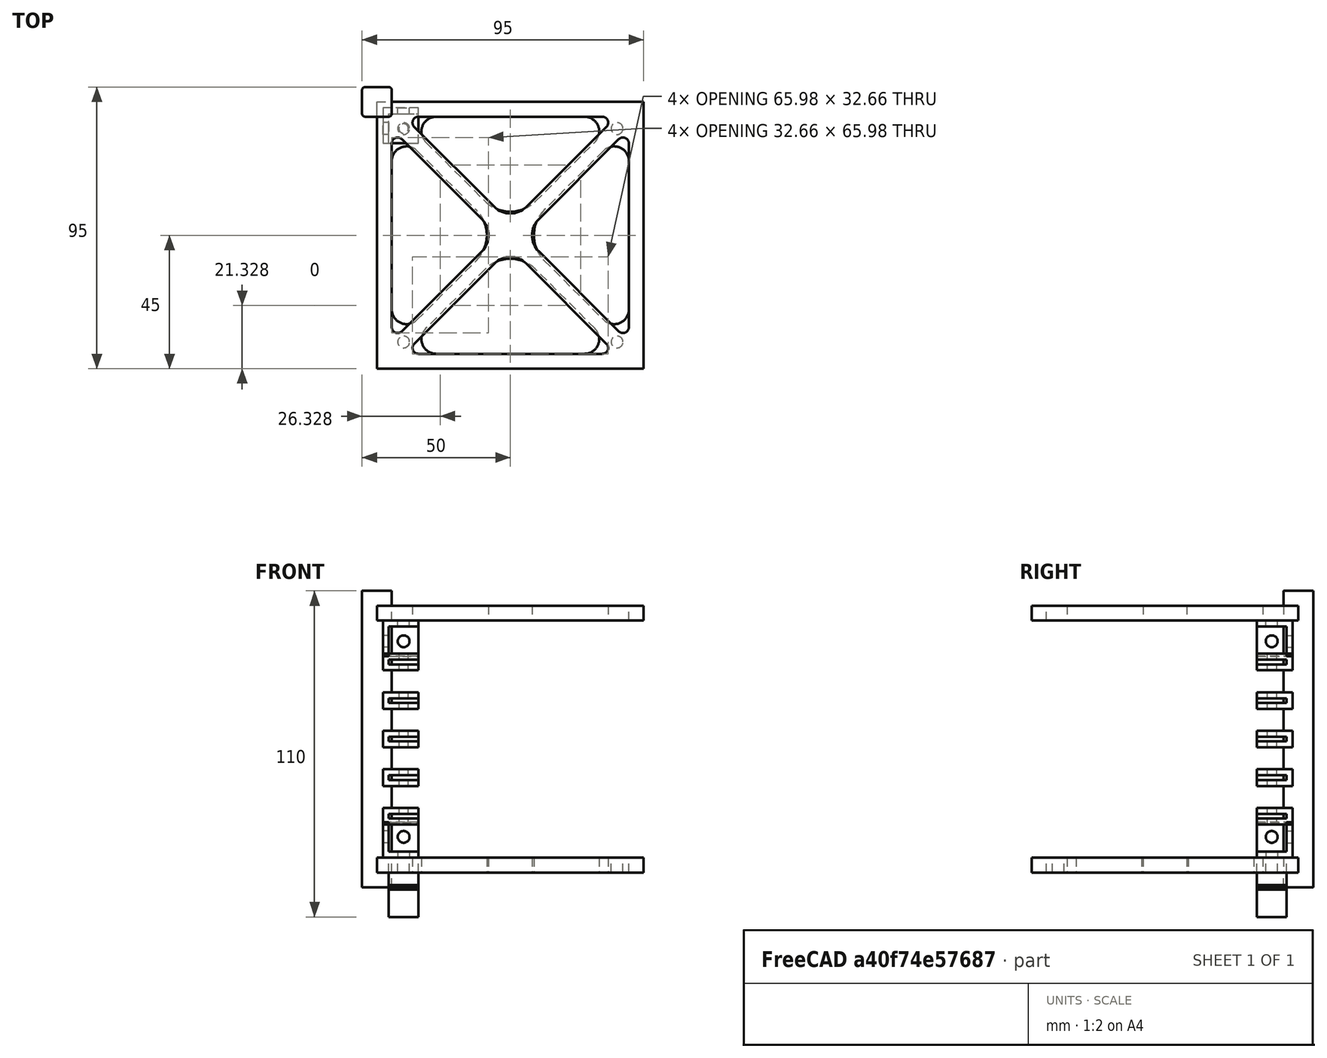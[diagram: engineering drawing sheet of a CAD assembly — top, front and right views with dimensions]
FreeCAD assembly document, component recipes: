
FREECAD ASSEMBLY — COMPONENT RECIPES ("cube")

This assembly document has 18 components, labeled P0..P17 below (a component is one placed body or linked part). 18 of them carry a construction recipe — the FreeCAD feature program that regenerates the part from scratch, quoted from this document or its linked companion documents; the rest are supplied as boundary geometry only. No exploded tour is included for this assembly.
COMPONENT P0 — recipe-attached ("BottomCutout", modeled in this document).
Construction recipe (the document's own serialized feature program — sketch geometry with constraints, then the solid features built on it; lengths are millimeters unless a unit is written):

FEATURE [Sketcher::SketchObject] Sketch
  FullyConstrained = true
  MapMode = 5
  Support = -> [XY_Plane001]
  sketch-geometry (28):
    g0: LineSegment StartX=-45 StartY=45 StartZ=0 EndX=45 EndY=45 EndZ=0
    g1: LineSegment StartX=45 StartY=45 StartZ=0 EndX=45 EndY=-45 EndZ=0
    g2: LineSegment StartX=45 StartY=-45 StartZ=0 EndX=-45 EndY=-45 EndZ=0
    g3: LineSegment StartX=-45 StartY=-45 StartZ=0 EndX=-45 EndY=45 EndZ=0
    g4: LineSegment StartX=-31 StartY=40 StartZ=0 EndX=31 EndY=40 EndZ=0
    g5: LineSegment StartX=-31 StartY=-40 StartZ=0 EndX=31 EndY=-40 EndZ=0
    g6: LineSegment StartX=-40 StartY=31 StartZ=0 EndX=-40 EndY=-31 EndZ=0
    g7: LineSegment StartX=40 StartY=31 StartZ=0 EndX=40 EndY=-31 EndZ=0
    g8: LineSegment StartX=-36.5858 StartY=32.4142 StartZ=0 EndX=-9.58579 EndY=5.41421 EndZ=0
    g9: LineSegment StartX=-32.4142 StartY=36.5858 StartZ=0 EndX=-5.41421 EndY=9.58579 EndZ=0
    g10: LineSegment StartX=5.41421 StartY=9.58579 StartZ=0 EndX=32.4142 EndY=36.5858 EndZ=0
    g11: LineSegment StartX=36.5858 StartY=32.4142 StartZ=0 EndX=9.58579 EndY=5.41421 EndZ=0
    g12: LineSegment StartX=9.58579 StartY=-5.41421 StartZ=0 EndX=36.5858 EndY=-32.4142 EndZ=0
    g13: LineSegment StartX=32.4142 StartY=-36.5858 StartZ=0 EndX=5.41421 EndY=-9.58579 EndZ=0
    g14: LineSegment StartX=-5.41421 StartY=-9.58579 StartZ=0 EndX=-32.4142 EndY=-36.5858 EndZ=0
    g15: LineSegment StartX=-36.5858 StartY=-32.4142 StartZ=0 EndX=-9.58579 EndY=-5.41421 EndZ=0
    g16: ArcOfCircle CenterX=38 CenterY=31 CenterZ=0 NormalX=0 NormalY=0 NormalZ=1 AngleXU=0 Radius=2 StartAngle=0 EndAngle=2.35619
    g17: ArcOfCircle CenterX=38 CenterY=-31 CenterZ=0 NormalX=0 NormalY=0 NormalZ=1 AngleXU=0 Radius=2 StartAngle=3.92699 EndAngle=6.28319
    g18: ArcOfCircle CenterX=31 CenterY=-38 CenterZ=0 NormalX=0 NormalY=0 NormalZ=1 AngleXU=0 Radius=2 StartAngle=4.71239 EndAngle=7.06858
    g19: ArcOfCircle CenterX=-31 CenterY=-38 CenterZ=0 NormalX=0 NormalY=0 NormalZ=1 AngleXU=0 Radius=2 StartAngle=2.35619 EndAngle=4.71239
    g20: ArcOfCircle CenterX=-38 CenterY=-31 CenterZ=0 NormalX=0 NormalY=0 NormalZ=1 AngleXU=0 Radius=2 StartAngle=3.14159 EndAngle=5.49779
    g21: ArcOfCircle CenterX=-38 CenterY=31 CenterZ=0 NormalX=0 NormalY=0 NormalZ=1 AngleXU=0 Radius=2 StartAngle=0.785398 EndAngle=3.14159
    g22: ArcOfCircle CenterX=-31 CenterY=38 CenterZ=0 NormalX=0 NormalY=0 NormalZ=1 AngleXU=0 Radius=2 StartAngle=1.5708 EndAngle=3.92699
    g23: ArcOfCircle CenterX=31 CenterY=38 CenterZ=0 NormalX=0 NormalY=0 NormalZ=1 AngleXU=0 Radius=2 StartAngle=5.49779 EndAngle=7.85398
    g24: ArcOfCircle CenterX=-15 CenterY=0 CenterZ=0 NormalX=0 NormalY=0 NormalZ=1 AngleXU=0 Radius=7.65685 StartAngle=5.49779 EndAngle=7.06858
    g25: ArcOfCircle CenterX=0 CenterY=15 CenterZ=0 NormalX=0 NormalY=0 NormalZ=1 AngleXU=0 Radius=7.65685 StartAngle=3.92699 EndAngle=5.49779
    g26: ArcOfCircle CenterX=15 CenterY=0 CenterZ=0 NormalX=0 NormalY=0 NormalZ=1 AngleXU=0 Radius=7.65685 StartAngle=2.35619 EndAngle=3.92699
    g27: ArcOfCircle CenterX=-6e-16 CenterY=-15 CenterZ=0 NormalX=0 NormalY=0 NormalZ=1 AngleXU=0 Radius=7.65685 StartAngle=0.785398 EndAngle=2.35619
  constraints (67):
    c: Coincident(g0,g1)
    c: Coincident(g1,g2)
    c: Coincident(g2,g3)
    c: Coincident(g3,g0)
    c: Horizontal(g0)
    c: Horizontal(g2)
    c: Vertical(g1)
    c: Vertical(g3)
    c: Symmetric(g0,g1,g-1)
    c: Equal(g2,g1)
    c: Horizontal(g4)
    c: Horizontal(g5)
    c: Vertical(g6)
    c: Vertical(g7)
    c: DistanceY(g3,g3) = 90
    c: Parallel(g8,g9)
    c: Parallel(g9,g12)
    c: Parallel(g12,g13)
    c: Parallel(g15,g14)
    c: Parallel(g14,g10)
    c: Parallel(g10,g11)
    c: Tangent(g11,g16) = -1.5708
    c: Tangent(g7,g16) = 1.5708
    c: Tangent(g12,g17) = -1.5708
    c: Tangent(g7,g17) = 1.5708
    c: Tangent(g13,g18) = -1.5708
    c: Tangent(g5,g18) = -1.5708
    c: Tangent(g14,g19) = -1.5708
    c: Tangent(g5,g19) = -1.5708
    c: Tangent(g15,g20) = -1.5708
    c: Tangent(g6,g20) = -1.5708
    c: Tangent(g6,g21) = -1.5708
    c: Tangent(g8,g21) = 1.5708
    c: Tangent(g9,g22) = -1.5708
    c: Tangent(g4,g22) = 1.5708
    c: Tangent(g4,g23) = 1.5708
    c: Tangent(g10,g23) = -1.5708
    c: Tangent(g8,g24) = 1.5708
    c: Tangent(g15,g24) = -1.5708
    c: Tangent(g9,g25) = -1.5708
    c: Tangent(g10,g25) = -1.5708
    c: Tangent(g11,g26) = -1.5708
    c: Tangent(g12,g26) = -1.5708
    c: Tangent(g13,g27) = -1.5708
    c: Tangent(g14,g27) = -1.5708
    c: Symmetric(g8,g12,g-1)
    c: PointOnObject(g24,g-1)
    c: PointOnObject(g26,g-1)
    c: Symmetric(g10,g14,g-1)
    c: Symmetric(g21,g17,g-1)
    c: Symmetric(g19,g23,g-1)
    c: Vertical(g21,g20)
    c: Horizontal(g18,g19)
    c: Vertical(g15,g8)
    c: Equal(g25,g24)
    c: Equal(g26,g27)
    c: PointOnObject(g25,g-2)
    c: Horizontal(g16,g21)
    c: Equal(g4,g5)
    c: Equal(g6,g5)
    c: DistanceX(g2,g6) = 5
    c: DistanceY(g2,g5) = 5
    c: DistanceX(g18,g1) = 14
    c: DistanceX(g26,g1) = 30
    c: DistanceY(g1,g18) = 7
    c: Perpendicular(g11,g8)
    c: DistanceX(g17,g1) = 7
FEATURE [PartDesign::Pad] Pad
  Direction = (1,1,1)
  Length = 5
  Length2 = 100
  Profile = -> Sketch
  Refine = true
  Type = 0
FEATURE [PartDesign::Body] Body  label="BottomCutout"
  Group = -> [Sketch,Pad]
  Origin = -> Origin001
  Placement = pos=(0,0,5) rot=(0,0,1;0rad)
  Tip = -> Pad
COMPONENT P1 — recipe-attached ("BottomCorner", modeled in this document).
Construction recipe (the document's own serialized feature program — sketch geometry with constraints, then the solid features built on it; lengths are millimeters unless a unit is written):

FEATURE [Sketcher::SketchObject] Sketch003
  FullyConstrained = true
  MapMode = 5
  Support = -> [XY_Plane004]
  sketch-geometry (4):
    g0: LineSegment StartX=-43 StartY=31 StartZ=0 EndX=-31 EndY=31 EndZ=0
    g1: LineSegment StartX=-31 StartY=31 StartZ=0 EndX=-31 EndY=43 EndZ=0
    g2: LineSegment StartX=-31 StartY=43 StartZ=0 EndX=-43 EndY=43 EndZ=0
    g3: LineSegment StartX=-43 StartY=43 StartZ=0 EndX=-43 EndY=31 EndZ=0
  constraints (12):
    c: Coincident(g1,g2)
    c: Coincident(g2,g3)
    c: Coincident(g3,g0)
    c: Horizontal(g0)
    c: Horizontal(g2)
    c: Vertical(g1)
    c: Vertical(g3)
    c: Equal(g3,g0)
    c: Coincident(g0,g1)
    c: Distance(g1,g0) = 12
    c: DistanceY(g-1,g0) = 31
    c: DistanceX(g0,g-1) = 31
FEATURE [PartDesign::Pad] Pad002
  Direction = (1,1,1)
  Length = 12
  Length2 = 100
  Profile = -> Sketch003
  Refine = true
  Reversed = true
  Type = 0
FEATURE [PartDesign::Boolean] Boolean001
  BaseFeature = -> Pad002
  Group = -> [Body003]
  Refine = true
  Type = 1
FEATURE [Sketcher::SketchObject] Sketch005  label="yCornerHoleSketch"
  FullyConstrained = true
  MapMode = 5
  Placement = pos=(0,0,0) rot=(1,0,0;1.5708rad)
  Support = -> [XZ_Plane004]
  sketch-geometry (1):
    g0: Circle CenterX=-36 CenterY=-5 CenterZ=0 NormalX=0 NormalY=0 NormalZ=1 AngleXU=0 Radius=2
  constraints (3):
    c: DistanceY(g0,g-1) = 5
    c: DistanceX(g-1,g0) = -36
    c: Radius(g0) = 2
FEATURE [PartDesign::Hole] Hole  label="yCornerHole"
  BaseFeature = -> Boolean001
  Depth = 25
  DepthType = 1
  Diameter = 4
  DrillForDepth = false
  DrillPoint = 1
  DrillPointAngle = 118
  HoleCutCountersinkAngle = 90
  HoleCutCustomValues = false
  HoleCutDepth = 0
  HoleCutDiameter = 4.1
  HoleCutType = 2
  ModelActualThread = false
  Profile = -> Sketch005
  Refine = true
  Tapered = false
  TaperedAngle = 90
  ThreadAngle = 0
  ThreadClass = 0
  ThreadCutOffInner = 0
  ThreadCutOffOuter = 0
  ThreadDirection = 0
  ThreadFit = 0
  ThreadPitch = 0
  ThreadSize = 0
  ThreadType = 0
  Threaded = false
FEATURE [Sketcher::SketchObject] Sketch006  label="zConerHoleSketch"
  FullyConstrained = true
  MapMode = 5
  Placement = pos=(0,0,-10) rot=(0,0,1;0rad)
  Support = -> [Hole]
  sketch-geometry (1):
    g0: Circle CenterX=-36 CenterY=36 CenterZ=0 NormalX=0 NormalY=0 NormalZ=1 AngleXU=0 Radius=2
  constraints (3):
    c: DistanceX(g-1,g0) = -36
    c: DistanceY(g-1,g0) = 36
    c: Radius(g0) = 2
FEATURE [PartDesign::Hole] Hole001  label="zCornerHole"
  BaseFeature = -> Hole
  Depth = 25
  DepthType = 0
  Diameter = 4
  DrillForDepth = false
  DrillPoint = 1
  DrillPointAngle = 118
  HoleCutCountersinkAngle = 90
  HoleCutCustomValues = false
  HoleCutDepth = 0
  HoleCutDiameter = 6.1
  HoleCutType = 0
  ModelActualThread = false
  Profile = -> Sketch006
  Refine = true
  Tapered = false
  TaperedAngle = 90
  ThreadAngle = 0
  ThreadClass = 0
  ThreadCutOffInner = 0
  ThreadCutOffOuter = 0
  ThreadDirection = 0
  ThreadFit = 0
  ThreadPitch = 0
  ThreadSize = 0
  ThreadType = 0
  Threaded = false
FEATURE [Sketcher::SketchObject] Sketch007  label="xCornerHoleSketch"
  FullyConstrained = true
  MapMode = 5
  Placement = pos=(-41,0,0) rot=(0.57735,0.57735,0.57735;2.0944rad)
  Support = -> [Hole001]
  sketch-geometry (1):
    g0: Circle CenterX=36 CenterY=-5 CenterZ=0 NormalX=0 NormalY=0 NormalZ=1 AngleXU=0 Radius=2
  constraints (3):
    c: DistanceY(g0,g-1) = 5
    c: DistanceX(g-1,g0) = 36
    c: Radius(g0) = 2
FEATURE [PartDesign::Hole] Hole002  label="xCornerHole"
  BaseFeature = -> Hole001
  Depth = 25
  DepthType = 0
  Diameter = 4
  DrillForDepth = false
  DrillPoint = 1
  DrillPointAngle = 118
  HoleCutCountersinkAngle = 90
  HoleCutCustomValues = false
  HoleCutDepth = 0
  HoleCutDiameter = 6.1
  HoleCutType = 0
  ModelActualThread = false
  Profile = -> Sketch007
  Refine = true
  Tapered = false
  TaperedAngle = 90
  ThreadAngle = 0
  ThreadClass = 0
  ThreadCutOffInner = 0
  ThreadCutOffOuter = 0
  ThreadDirection = 0
  ThreadFit = 0
  ThreadPitch = 0
  ThreadSize = 0
  ThreadType = 0
  Threaded = false
FEATURE [PartDesign::Body] Body002  label="BottomCorner"
  Group = -> [Sketch003,Pad002,Boolean001,Sketch005,Hole,Sketch006,Hole001,Sketch007,Hole002]
  Origin = -> Origin004
  Placement = pos=(0,0,22) rot=(0,0,1;0rad)
  Tip = -> Hole002
COMPONENT P2 — recipe-attached ("Neg_Corner", modeled in this document).
Construction recipe (the document's own serialized feature program — sketch geometry with constraints, then the solid features built on it; lengths are millimeters unless a unit is written):

FEATURE [Sketcher::SketchObject] Sketch002
  FullyConstrained = true
  MapMode = 5
  Support = -> [XY_Plane005]
  sketch-geometry (4):
    g0: LineSegment StartX=-41 StartY=41 StartZ=0 EndX=-31 EndY=41 EndZ=0
    g1: LineSegment StartX=-31 StartY=41 StartZ=0 EndX=-31 EndY=31 EndZ=0
    g2: LineSegment StartX=-31 StartY=31 StartZ=0 EndX=-41 EndY=31 EndZ=0
    g3: LineSegment StartX=-41 StartY=31 StartZ=0 EndX=-41 EndY=41 EndZ=0
  constraints (12):
    c: Coincident(g0,g1)
    c: Coincident(g1,g2)
    c: Coincident(g2,g3)
    c: Coincident(g3,g0)
    c: Horizontal(g0)
    c: Horizontal(g2)
    c: Vertical(g1)
    c: Vertical(g3)
    c: Equal(g3,g2)
    c: Distance(g1) = 10
    c: DistanceX(g-1,g2) = -41
    c: DistanceY(g-1,g2) = 31
FEATURE [PartDesign::Pad] Pad003
  Direction = (1,1,1)
  Length = 10
  Length2 = 100
  Profile = -> Sketch002
  Refine = true
  Reversed = true
  Type = 0
FEATURE [PartDesign::Body] Body003  label="Neg_Corner"
  Group = -> [Sketch002,Pad003]
  Origin = -> Origin005
  Tip = -> Pad003
COMPONENT P3 — recipe-attached ("TopCutout", modeled in this document).
Construction recipe (the document's own serialized feature program — sketch geometry with constraints, then the solid features built on it; lengths are millimeters unless a unit is written):

FEATURE [Sketcher::SketchObject] Sketch010
  FullyConstrained = true
  MapMode = 5
  Support = -> [XY_Plane008]
  sketch-geometry (28):
    g0: LineSegment StartX=-45 StartY=45 StartZ=0 EndX=45 EndY=45 EndZ=0
    g1: LineSegment StartX=45 StartY=45 StartZ=0 EndX=45 EndY=-45 EndZ=0
    g2: LineSegment StartX=45 StartY=-45 StartZ=0 EndX=-45 EndY=-45 EndZ=0
    g3: LineSegment StartX=-45 StartY=-45 StartZ=0 EndX=-45 EndY=45 EndZ=0
    g4: LineSegment StartX=-31 StartY=40 StartZ=0 EndX=31 EndY=40 EndZ=0
    g5: LineSegment StartX=-31 StartY=-40 StartZ=0 EndX=31 EndY=-40 EndZ=0
    g6: LineSegment StartX=-40 StartY=31 StartZ=0 EndX=-40 EndY=-31 EndZ=0
    g7: LineSegment StartX=40 StartY=31 StartZ=0 EndX=40 EndY=-31 EndZ=0
    g8: LineSegment StartX=-36.5858 StartY=32.4142 StartZ=0 EndX=-9.58579 EndY=5.41421 EndZ=0
    g9: LineSegment StartX=-32.4142 StartY=36.5858 StartZ=0 EndX=-5.41421 EndY=9.58579 EndZ=0
    g10: LineSegment StartX=5.41421 StartY=9.58579 StartZ=0 EndX=32.4142 EndY=36.5858 EndZ=0
    g11: LineSegment StartX=36.5858 StartY=32.4142 StartZ=0 EndX=9.58579 EndY=5.41421 EndZ=0
    g12: LineSegment StartX=9.58579 StartY=-5.41421 StartZ=0 EndX=36.5858 EndY=-32.4142 EndZ=0
    g13: LineSegment StartX=32.4142 StartY=-36.5858 StartZ=0 EndX=5.41421 EndY=-9.58579 EndZ=0
    g14: LineSegment StartX=-5.41421 StartY=-9.58579 StartZ=0 EndX=-32.4142 EndY=-36.5858 EndZ=0
    g15: LineSegment StartX=-36.5858 StartY=-32.4142 StartZ=0 EndX=-9.58579 EndY=-5.41421 EndZ=0
    g16: ArcOfCircle CenterX=38 CenterY=31 CenterZ=0 NormalX=0 NormalY=0 NormalZ=1 AngleXU=0 Radius=2 StartAngle=0 EndAngle=2.35619
    g17: ArcOfCircle CenterX=38 CenterY=-31 CenterZ=0 NormalX=0 NormalY=0 NormalZ=1 AngleXU=0 Radius=2 StartAngle=3.92699 EndAngle=6.28319
    g18: ArcOfCircle CenterX=31 CenterY=-38 CenterZ=0 NormalX=0 NormalY=0 NormalZ=1 AngleXU=0 Radius=2 StartAngle=4.71239 EndAngle=7.06858
    g19: ArcOfCircle CenterX=-31 CenterY=-38 CenterZ=0 NormalX=0 NormalY=0 NormalZ=1 AngleXU=0 Radius=2 StartAngle=2.35619 EndAngle=4.71239
    g20: ArcOfCircle CenterX=-38 CenterY=-31 CenterZ=0 NormalX=0 NormalY=0 NormalZ=1 AngleXU=0 Radius=2 StartAngle=3.14159 EndAngle=5.49779
    g21: ArcOfCircle CenterX=-38 CenterY=31 CenterZ=0 NormalX=0 NormalY=0 NormalZ=1 AngleXU=0 Radius=2 StartAngle=0.785398 EndAngle=3.14159
    g22: ArcOfCircle CenterX=-31 CenterY=38 CenterZ=0 NormalX=0 NormalY=0 NormalZ=1 AngleXU=0 Radius=2 StartAngle=1.5708 EndAngle=3.92699
    g23: ArcOfCircle CenterX=31 CenterY=38 CenterZ=0 NormalX=0 NormalY=0 NormalZ=1 AngleXU=0 Radius=2 StartAngle=5.49779 EndAngle=7.85398
    g24: ArcOfCircle CenterX=-15 CenterY=0 CenterZ=0 NormalX=0 NormalY=0 NormalZ=1 AngleXU=0 Radius=7.65685 StartAngle=5.49779 EndAngle=7.06858
    g25: ArcOfCircle CenterX=0 CenterY=15 CenterZ=0 NormalX=0 NormalY=0 NormalZ=1 AngleXU=0 Radius=7.65685 StartAngle=3.92699 EndAngle=5.49779
    g26: ArcOfCircle CenterX=15 CenterY=0 CenterZ=0 NormalX=0 NormalY=0 NormalZ=1 AngleXU=0 Radius=7.65685 StartAngle=2.35619 EndAngle=3.92699
    g27: ArcOfCircle CenterX=-6e-16 CenterY=-15 CenterZ=0 NormalX=0 NormalY=0 NormalZ=1 AngleXU=0 Radius=7.65685 StartAngle=0.785398 EndAngle=2.35619
  constraints (67):
    c: Coincident(g0,g1)
    c: Coincident(g1,g2)
    c: Coincident(g2,g3)
    c: Coincident(g3,g0)
    c: Horizontal(g0)
    c: Horizontal(g2)
    c: Vertical(g1)
    c: Vertical(g3)
    c: Symmetric(g0,g1,g-1)
    c: Equal(g2,g1)
    c: Horizontal(g4)
    c: Horizontal(g5)
    c: Vertical(g6)
    c: Vertical(g7)
    c: DistanceY(g3,g3) = 90
    c: Parallel(g8,g9)
    c: Parallel(g9,g12)
    c: Parallel(g12,g13)
    c: Parallel(g15,g14)
    c: Parallel(g14,g10)
    c: Parallel(g10,g11)
    c: Tangent(g11,g16) = -1.5708
    c: Tangent(g7,g16) = 1.5708
    c: Tangent(g12,g17) = -1.5708
    c: Tangent(g7,g17) = 1.5708
    c: Tangent(g13,g18) = -1.5708
    c: Tangent(g5,g18) = -1.5708
    c: Tangent(g14,g19) = -1.5708
    c: Tangent(g5,g19) = -1.5708
    c: Tangent(g15,g20) = -1.5708
    c: Tangent(g6,g20) = -1.5708
    c: Tangent(g6,g21) = -1.5708
    c: Tangent(g8,g21) = 1.5708
    c: Tangent(g9,g22) = -1.5708
    c: Tangent(g4,g22) = 1.5708
    c: Tangent(g4,g23) = 1.5708
    c: Tangent(g10,g23) = -1.5708
    c: Tangent(g8,g24) = 1.5708
    c: Tangent(g15,g24) = -1.5708
    c: Tangent(g9,g25) = -1.5708
    c: Tangent(g10,g25) = -1.5708
    c: Tangent(g11,g26) = -1.5708
    c: Tangent(g12,g26) = -1.5708
    c: Tangent(g13,g27) = -1.5708
    c: Tangent(g14,g27) = -1.5708
    c: Symmetric(g8,g12,g-1)
    c: PointOnObject(g24,g-1)
    c: PointOnObject(g26,g-1)
    c: Symmetric(g10,g14,g-1)
    c: Symmetric(g21,g17,g-1)
    c: Symmetric(g19,g23,g-1)
    c: Vertical(g21,g20)
    c: Horizontal(g18,g19)
    c: Vertical(g15,g8)
    c: Equal(g25,g24)
    c: Equal(g26,g27)
    c: PointOnObject(g25,g-2)
    c: Horizontal(g16,g21)
    c: Equal(g4,g5)
    c: Equal(g6,g5)
    c: DistanceX(g2,g6) = 5
    c: DistanceY(g2,g5) = 5
    c: DistanceX(g18,g1) = 14
    c: DistanceX(g26,g1) = 30
    c: DistanceY(g1,g18) = 7
    c: Perpendicular(g11,g8)
    c: DistanceX(g17,g1) = 7
FEATURE [PartDesign::Pad] Pad005
  Direction = (1,1,1)
  Length = 5
  Length2 = 100
  Profile = -> Sketch010
  Refine = true
  Type = 0
FEATURE [PartDesign::Body] Body005  label="TopCutout"
  Group = -> [Sketch010,Pad005]
  Origin = -> Origin008
  Placement = pos=(0,0,90) rot=(0,0,1;0rad)
  Tip = -> Pad005
COMPONENT P4 — recipe-attached ("TopCorner", modeled in this document).
Construction recipe (the document's own serialized feature program — sketch geometry with constraints, then the solid features built on it; lengths are millimeters unless a unit is written):

FEATURE [Sketcher::SketchObject] Sketch012
  FullyConstrained = true
  MapMode = 5
  Support = -> [XY_Plane009]
  sketch-geometry (4):
    g0: LineSegment StartX=-43 StartY=31 StartZ=0 EndX=-31 EndY=31 EndZ=0
    g1: LineSegment StartX=-31 StartY=31 StartZ=0 EndX=-31 EndY=43 EndZ=0
    g2: LineSegment StartX=-31 StartY=43 StartZ=0 EndX=-43 EndY=43 EndZ=0
    g3: LineSegment StartX=-43 StartY=43 StartZ=0 EndX=-43 EndY=31 EndZ=0
  constraints (12):
    c: Coincident(g1,g2)
    c: Coincident(g2,g3)
    c: Coincident(g3,g0)
    c: Horizontal(g0)
    c: Horizontal(g2)
    c: Vertical(g1)
    c: Vertical(g3)
    c: Equal(g3,g0)
    c: Coincident(g0,g1)
    c: Distance(g1,g0) = 12
    c: DistanceY(g-1,g0) = 31
    c: DistanceX(g0,g-1) = 31
FEATURE [PartDesign::Pad] Pad006
  Direction = (1,1,1)
  Length = 12
  Length2 = 100
  Profile = -> Sketch012
  Refine = true
  Type = 0
FEATURE [PartDesign::Boolean] Boolean003
  BaseFeature = -> Pad006
  Group = -> [Body007]
  Refine = true
  Type = 1
FEATURE [Sketcher::SketchObject] Sketch013  label="yCornerHoleSketch001"
  FullyConstrained = true
  MapMode = 5
  Placement = pos=(0,0,0) rot=(1,0,0;1.5708rad)
  Support = -> [XZ_Plane009]
  sketch-geometry (1):
    g0: Circle CenterX=-36 CenterY=5 CenterZ=0 NormalX=0 NormalY=0 NormalZ=1 AngleXU=0 Radius=2
  constraints (3):
    c: DistanceY(g0,g-1) = -5
    c: DistanceX(g-1,g0) = -36
    c: Radius(g0) = 2
FEATURE [PartDesign::Hole] Hole005  label="yCornerHole001"
  BaseFeature = -> Boolean003
  Depth = 25
  DepthType = 1
  Diameter = 4
  DrillForDepth = false
  DrillPoint = 1
  DrillPointAngle = 118
  HoleCutCountersinkAngle = 90
  HoleCutCustomValues = false
  HoleCutDepth = 0
  HoleCutDiameter = 4.1
  HoleCutType = 2
  ModelActualThread = false
  Profile = -> Sketch013
  Refine = true
  Tapered = false
  TaperedAngle = 90
  ThreadAngle = 0
  ThreadClass = 0
  ThreadCutOffInner = 0
  ThreadCutOffOuter = 0
  ThreadDirection = 0
  ThreadFit = 0
  ThreadPitch = 0
  ThreadSize = 0
  ThreadType = 0
  Threaded = false
FEATURE [Sketcher::SketchObject] Sketch014  label="zConerHoleSketch001"
  FullyConstrained = true
  MapMode = 5
  Placement = pos=(0,0,10) rot=(1,0,0;3.14159rad)
  Support = -> [Hole005]
  sketch-geometry (1):
    g0: Circle CenterX=-36 CenterY=-36 CenterZ=0 NormalX=0 NormalY=0 NormalZ=1 AngleXU=0 Radius=2
  constraints (3):
    c: DistanceX(g-1,g0) = -36
    c: DistanceY(g-1,g0) = -36
    c: Radius(g0) = 2
FEATURE [PartDesign::Hole] Hole006  label="zCornerHole001"
  BaseFeature = -> Hole005
  Depth = 25
  DepthType = 0
  Diameter = 4
  DrillForDepth = false
  DrillPoint = 1
  DrillPointAngle = 118
  HoleCutCountersinkAngle = 90
  HoleCutCustomValues = false
  HoleCutDepth = 0
  HoleCutDiameter = 6.1
  HoleCutType = 0
  ModelActualThread = false
  Profile = -> Sketch014
  Refine = true
  Tapered = false
  TaperedAngle = 90
  ThreadAngle = 0
  ThreadClass = 0
  ThreadCutOffInner = 0
  ThreadCutOffOuter = 0
  ThreadDirection = 0
  ThreadFit = 0
  ThreadPitch = 0
  ThreadSize = 0
  ThreadType = 0
  Threaded = false
FEATURE [Sketcher::SketchObject] Sketch015  label="xCornerHoleSketch001"
  FullyConstrained = true
  MapMode = 5
  Placement = pos=(-41,0,0) rot=(0.57735,0.57735,0.57735;2.0944rad)
  Support = -> [Hole006]
  sketch-geometry (1):
    g0: Circle CenterX=36 CenterY=5 CenterZ=0 NormalX=0 NormalY=0 NormalZ=1 AngleXU=0 Radius=2
  constraints (3):
    c: DistanceY(g0,g-1) = -5
    c: DistanceX(g-1,g0) = 36
    c: Radius(g0) = 2
FEATURE [PartDesign::Hole] Hole007  label="xCornerHole001"
  BaseFeature = -> Hole006
  Depth = 25
  DepthType = 0
  Diameter = 4
  DrillForDepth = false
  DrillPoint = 1
  DrillPointAngle = 118
  HoleCutCountersinkAngle = 90
  HoleCutCustomValues = false
  HoleCutDepth = 0
  HoleCutDiameter = 6.1
  HoleCutType = 0
  ModelActualThread = false
  Profile = -> Sketch015
  Refine = true
  Tapered = false
  TaperedAngle = 90
  ThreadAngle = 0
  ThreadClass = 0
  ThreadCutOffInner = 0
  ThreadCutOffOuter = 0
  ThreadDirection = 0
  ThreadFit = 0
  ThreadPitch = 0
  ThreadSize = 0
  ThreadType = 0
  Threaded = false
FEATURE [PartDesign::Body] Body006  label="TopCorner"
  Group = -> [Sketch012,Pad006,Boolean003,Sketch013,Hole005,Sketch014,Hole006,Sketch015,Hole007]
  Origin = -> Origin009
  Placement = pos=(0,0,78) rot=(0,1,0;0rad)
  Tip = -> Hole007
COMPONENT P5 — recipe-attached ("Neg_Corner001", modeled in this document).
Construction recipe (the document's own serialized feature program — sketch geometry with constraints, then the solid features built on it; lengths are millimeters unless a unit is written):

FEATURE [Sketcher::SketchObject] Sketch011
  FullyConstrained = true
  MapMode = 5
  Support = -> [XY_Plane010]
  sketch-geometry (4):
    g0: LineSegment StartX=-41 StartY=41 StartZ=0 EndX=-31 EndY=41 EndZ=0
    g1: LineSegment StartX=-31 StartY=41 StartZ=0 EndX=-31 EndY=31 EndZ=0
    g2: LineSegment StartX=-31 StartY=31 StartZ=0 EndX=-41 EndY=31 EndZ=0
    g3: LineSegment StartX=-41 StartY=31 StartZ=0 EndX=-41 EndY=41 EndZ=0
  constraints (12):
    c: Coincident(g0,g1)
    c: Coincident(g1,g2)
    c: Coincident(g2,g3)
    c: Coincident(g3,g0)
    c: Horizontal(g0)
    c: Horizontal(g2)
    c: Vertical(g1)
    c: Vertical(g3)
    c: Equal(g3,g2)
    c: Distance(g1) = 10
    c: DistanceX(g-1,g2) = -41
    c: DistanceY(g-1,g2) = 31
FEATURE [PartDesign::Pad] Pad007
  Direction = (1,1,1)
  Length = 10
  Length2 = 100
  Profile = -> Sketch011
  Refine = true
  Type = 0
FEATURE [PartDesign::Body] Body007  label="Neg_Corner001"
  Group = -> [Sketch011,Pad007]
  Origin = -> Origin010
  Tip = -> Pad007
COMPONENT P6 — recipe-attached ("BoardSupport", modeled in this document).
Construction recipe (the document's own serialized feature program — sketch geometry with constraints, then the solid features built on it; lengths are millimeters unless a unit is written):

FEATURE [Sketcher::SketchObject] Sketch017
  FullyConstrained = true
  MapMode = 5
  Support = -> [XY_Plane011]
  sketch-geometry (5):
    g0: Circle CenterX=-36 CenterY=36 CenterZ=0 NormalX=0 NormalY=0 NormalZ=1 AngleXU=0 Radius=1.62
    g1: LineSegment StartX=-43 StartY=31 StartZ=0 EndX=-31 EndY=31 EndZ=0
    g2: LineSegment StartX=-31 StartY=31 StartZ=0 EndX=-31 EndY=43 EndZ=0
    g3: LineSegment StartX=-31 StartY=43 StartZ=0 EndX=-43 EndY=43 EndZ=0
    g4: LineSegment StartX=-43 StartY=43 StartZ=0 EndX=-43 EndY=31 EndZ=0
  constraints (15):
    c: Radius(g0) = 1.62
    c: Coincident(g1,g2)
    c: Coincident(g2,g3)
    c: Coincident(g3,g4)
    c: Coincident(g4,g1)
    c: Horizontal(g1)
    c: Horizontal(g3)
    c: Vertical(g2)
    c: Vertical(g4)
    c: Equal(g4,g1)
    c: Distance(g2) = 12
    c: DistanceX(g0,g-1) = 36
    c: DistanceY(g-1,g0) = 36
    c: DistanceY(g1,g0) = 5
    c: DistanceX(g0,g1) = 5
FEATURE [PartDesign::Pad] Pad009
  Direction = (1,1,1)
  Length = 5.6
  Length2 = 100
  Midplane = true
  Profile = -> Sketch017
  Refine = true
  Type = 0
FEATURE [PartDesign::Boolean] Boolean004
  BaseFeature = -> Pad009
  Group = -> [Body009]
  Refine = true
  Type = 1
FEATURE [PartDesign::Body] Body008  label="BoardSupport"
  Group = -> [Sketch017,Pad009,Boolean004]
  Origin = -> Origin011
  Placement = pos=(0,0,76) rot=(0,0,1;0rad)
  Tip = -> Boolean004
COMPONENT P7 — recipe-attached ("BoardPositive", modeled in this document).
Construction recipe (the document's own serialized feature program — sketch geometry with constraints, then the solid features built on it; lengths are millimeters unless a unit is written):

FEATURE [Sketcher::SketchObject] Sketch016
  FullyConstrained = true
  MapMode = 5
  Support = -> [XY_Plane012]
  sketch-geometry (5):
    g0: Circle CenterX=-36 CenterY=36 CenterZ=0 NormalX=0 NormalY=0 NormalZ=1 AngleXU=0 Radius=1.62
    g1: LineSegment StartX=-41 StartY=31 StartZ=0 EndX=-31 EndY=31 EndZ=0
    g2: LineSegment StartX=-31 StartY=31 StartZ=0 EndX=-31 EndY=41 EndZ=0
    g3: LineSegment StartX=-31 StartY=41 StartZ=0 EndX=-41 EndY=41 EndZ=0
    g4: LineSegment StartX=-41 StartY=41 StartZ=0 EndX=-41 EndY=31 EndZ=0
  constraints (14):
    c: Radius(g0) = 1.62
    c: Coincident(g1,g2)
    c: Coincident(g2,g3)
    c: Coincident(g3,g4)
    c: Coincident(g4,g1)
    c: Horizontal(g1)
    c: Horizontal(g3)
    c: Vertical(g2)
    c: Vertical(g4)
    c: Equal(g4,g1)
    c: Distance(g2) = 10
    c: Symmetric(g3,g1,g0)
    c: DistanceX(g0,g-1) = 36
    c: DistanceY(g-1,g0) = 36
FEATURE [PartDesign::Pad] Pad008
  Direction = (1,1,1)
  Length = 1.6
  Length2 = 100
  Profile = -> Sketch016
  Refine = true
  Type = 0
FEATURE [PartDesign::Body] Body009  label="BoardPositive"
  Group = -> [Sketch016,Pad008]
  Origin = -> Origin012
  Placement = pos=(0,0,-0.8) rot=(0,0,1;0rad)
  Tip = -> Pad008
COMPONENT P8 — recipe-attached ("BoardSupport001", modeled in this document).
Construction recipe (the document's own serialized feature program — sketch geometry with constraints, then the solid features built on it; lengths are millimeters unless a unit is written):

FEATURE [Sketcher::SketchObject] Sketch019
  FullyConstrained = true
  MapMode = 5
  Support = -> [XY_Plane014]
  sketch-geometry (5):
    g0: Circle CenterX=-36 CenterY=36 CenterZ=0 NormalX=0 NormalY=0 NormalZ=1 AngleXU=0 Radius=1.62
    g1: LineSegment StartX=-43 StartY=31 StartZ=0 EndX=-31 EndY=31 EndZ=0
    g2: LineSegment StartX=-31 StartY=31 StartZ=0 EndX=-31 EndY=43 EndZ=0
    g3: LineSegment StartX=-31 StartY=43 StartZ=0 EndX=-43 EndY=43 EndZ=0
    g4: LineSegment StartX=-43 StartY=43 StartZ=0 EndX=-43 EndY=31 EndZ=0
  constraints (15):
    c: Radius(g0) = 1.62
    c: Coincident(g1,g2)
    c: Coincident(g2,g3)
    c: Coincident(g3,g4)
    c: Coincident(g4,g1)
    c: Horizontal(g1)
    c: Horizontal(g3)
    c: Vertical(g2)
    c: Vertical(g4)
    c: Equal(g4,g1)
    c: Distance(g2) = 12
    c: DistanceX(g0,g-1) = 36
    c: DistanceY(g-1,g0) = 36
    c: DistanceY(g1,g0) = 5
    c: DistanceX(g0,g1) = 5
FEATURE [PartDesign::Pad] Pad011
  Direction = (1,1,1)
  Length = 5.6
  Length2 = 100
  Midplane = true
  Profile = -> Sketch019
  Refine = true
  Type = 0
FEATURE [PartDesign::Boolean] Boolean005
  BaseFeature = -> Pad011
  Group = -> [Body011]
  Refine = true
  Type = 1
FEATURE [PartDesign::Body] Body010  label="BoardSupport001"
  Group = -> [Sketch019,Pad011,Boolean005]
  Origin = -> Origin013
  Placement = pos=(0,0,63) rot=(0,0,1;0rad)
  Tip = -> Boolean005
COMPONENT P9 — recipe-attached ("BoardPositive001", modeled in this document).
Construction recipe (the document's own serialized feature program — sketch geometry with constraints, then the solid features built on it; lengths are millimeters unless a unit is written):

FEATURE [Sketcher::SketchObject] Sketch018
  FullyConstrained = true
  MapMode = 5
  Support = -> [XY_Plane015]
  sketch-geometry (5):
    g0: Circle CenterX=-36 CenterY=36 CenterZ=0 NormalX=0 NormalY=0 NormalZ=1 AngleXU=0 Radius=1.62
    g1: LineSegment StartX=-41 StartY=31 StartZ=0 EndX=-31 EndY=31 EndZ=0
    g2: LineSegment StartX=-31 StartY=31 StartZ=0 EndX=-31 EndY=41 EndZ=0
    g3: LineSegment StartX=-31 StartY=41 StartZ=0 EndX=-41 EndY=41 EndZ=0
    g4: LineSegment StartX=-41 StartY=41 StartZ=0 EndX=-41 EndY=31 EndZ=0
  constraints (14):
    c: Radius(g0) = 1.62
    c: Coincident(g1,g2)
    c: Coincident(g2,g3)
    c: Coincident(g3,g4)
    c: Coincident(g4,g1)
    c: Horizontal(g1)
    c: Horizontal(g3)
    c: Vertical(g2)
    c: Vertical(g4)
    c: Equal(g4,g1)
    c: Distance(g2) = 10
    c: Symmetric(g3,g1,g0)
    c: DistanceX(g0,g-1) = 36
    c: DistanceY(g-1,g0) = 36
FEATURE [PartDesign::Pad] Pad010
  Direction = (1,1,1)
  Length = 1.6
  Length2 = 100
  Profile = -> Sketch018
  Refine = true
  Type = 0
FEATURE [PartDesign::Body] Body011  label="BoardPositive001"
  Group = -> [Sketch018,Pad010]
  Origin = -> Origin014
  Placement = pos=(0,0,-0.8) rot=(0,0,1;0rad)
  Tip = -> Pad010
COMPONENT P10 — recipe-attached ("BoardSupport002", modeled in this document).
Construction recipe (the document's own serialized feature program — sketch geometry with constraints, then the solid features built on it; lengths are millimeters unless a unit is written):

FEATURE [Sketcher::SketchObject] Sketch021
  FullyConstrained = true
  MapMode = 5
  Support = -> [XY_Plane016]
  sketch-geometry (5):
    g0: Circle CenterX=-36 CenterY=36 CenterZ=0 NormalX=0 NormalY=0 NormalZ=1 AngleXU=0 Radius=1.62
    g1: LineSegment StartX=-43 StartY=31 StartZ=0 EndX=-31 EndY=31 EndZ=0
    g2: LineSegment StartX=-31 StartY=31 StartZ=0 EndX=-31 EndY=43 EndZ=0
    g3: LineSegment StartX=-31 StartY=43 StartZ=0 EndX=-43 EndY=43 EndZ=0
    g4: LineSegment StartX=-43 StartY=43 StartZ=0 EndX=-43 EndY=31 EndZ=0
  constraints (15):
    c: Radius(g0) = 1.62
    c: Coincident(g1,g2)
    c: Coincident(g2,g3)
    c: Coincident(g3,g4)
    c: Coincident(g4,g1)
    c: Horizontal(g1)
    c: Horizontal(g3)
    c: Vertical(g2)
    c: Vertical(g4)
    c: Equal(g4,g1)
    c: Distance(g2) = 12
    c: DistanceX(g0,g-1) = 36
    c: DistanceY(g-1,g0) = 36
    c: DistanceY(g1,g0) = 5
    c: DistanceX(g0,g1) = 5
FEATURE [PartDesign::Pad] Pad013
  Direction = (1,1,1)
  Length = 5.6
  Length2 = 100
  Midplane = true
  Profile = -> Sketch021
  Refine = true
  Type = 0
FEATURE [PartDesign::Boolean] Boolean006
  BaseFeature = -> Pad013
  Group = -> [Body013]
  Refine = true
  Type = 1
FEATURE [PartDesign::Body] Body012  label="BoardSupport002"
  Group = -> [Sketch021,Pad013,Boolean006]
  Origin = -> Origin015
  Placement = pos=(0,0,50) rot=(0,0,1;0rad)
  Tip = -> Boolean006
COMPONENT P11 — recipe-attached ("BoardPositive002", modeled in this document).
Construction recipe (the document's own serialized feature program — sketch geometry with constraints, then the solid features built on it; lengths are millimeters unless a unit is written):

FEATURE [Sketcher::SketchObject] Sketch020
  FullyConstrained = true
  MapMode = 5
  Support = -> [XY_Plane017]
  sketch-geometry (5):
    g0: Circle CenterX=-36 CenterY=36 CenterZ=0 NormalX=0 NormalY=0 NormalZ=1 AngleXU=0 Radius=1.62
    g1: LineSegment StartX=-41 StartY=31 StartZ=0 EndX=-31 EndY=31 EndZ=0
    g2: LineSegment StartX=-31 StartY=31 StartZ=0 EndX=-31 EndY=41 EndZ=0
    g3: LineSegment StartX=-31 StartY=41 StartZ=0 EndX=-41 EndY=41 EndZ=0
    g4: LineSegment StartX=-41 StartY=41 StartZ=0 EndX=-41 EndY=31 EndZ=0
  constraints (14):
    c: Radius(g0) = 1.62
    c: Coincident(g1,g2)
    c: Coincident(g2,g3)
    c: Coincident(g3,g4)
    c: Coincident(g4,g1)
    c: Horizontal(g1)
    c: Horizontal(g3)
    c: Vertical(g2)
    c: Vertical(g4)
    c: Equal(g4,g1)
    c: Distance(g2) = 10
    c: Symmetric(g3,g1,g0)
    c: DistanceX(g0,g-1) = 36
    c: DistanceY(g-1,g0) = 36
FEATURE [PartDesign::Pad] Pad012
  Direction = (1,1,1)
  Length = 1.6
  Length2 = 100
  Profile = -> Sketch020
  Refine = true
  Type = 0
FEATURE [PartDesign::Body] Body013  label="BoardPositive002"
  Group = -> [Sketch020,Pad012]
  Origin = -> Origin016
  Placement = pos=(0,0,-0.8) rot=(0,0,1;0rad)
  Tip = -> Pad012
COMPONENT P12 — recipe-attached ("BoardSupport003", modeled in this document).
Construction recipe (the document's own serialized feature program — sketch geometry with constraints, then the solid features built on it; lengths are millimeters unless a unit is written):

FEATURE [Sketcher::SketchObject] Sketch023
  FullyConstrained = true
  MapMode = 5
  Support = -> [XY_Plane018]
  sketch-geometry (5):
    g0: Circle CenterX=-36 CenterY=36 CenterZ=0 NormalX=0 NormalY=0 NormalZ=1 AngleXU=0 Radius=1.62
    g1: LineSegment StartX=-43 StartY=31 StartZ=0 EndX=-31 EndY=31 EndZ=0
    g2: LineSegment StartX=-31 StartY=31 StartZ=0 EndX=-31 EndY=43 EndZ=0
    g3: LineSegment StartX=-31 StartY=43 StartZ=0 EndX=-43 EndY=43 EndZ=0
    g4: LineSegment StartX=-43 StartY=43 StartZ=0 EndX=-43 EndY=31 EndZ=0
  constraints (15):
    c: Radius(g0) = 1.62
    c: Coincident(g1,g2)
    c: Coincident(g2,g3)
    c: Coincident(g3,g4)
    c: Coincident(g4,g1)
    c: Horizontal(g1)
    c: Horizontal(g3)
    c: Vertical(g2)
    c: Vertical(g4)
    c: Equal(g4,g1)
    c: Distance(g2) = 12
    c: DistanceX(g0,g-1) = 36
    c: DistanceY(g-1,g0) = 36
    c: DistanceY(g1,g0) = 5
    c: DistanceX(g0,g1) = 5
FEATURE [PartDesign::Pad] Pad015
  Direction = (1,1,1)
  Length = 5.6
  Length2 = 100
  Midplane = true
  Profile = -> Sketch023
  Refine = true
  Type = 0
FEATURE [PartDesign::Boolean] Boolean007
  BaseFeature = -> Pad015
  Group = -> [Body015]
  Refine = true
  Type = 1
FEATURE [PartDesign::Body] Body014  label="BoardSupport003"
  Group = -> [Sketch023,Pad015,Boolean007]
  Origin = -> Origin017
  Placement = pos=(0,0,37) rot=(0,0,1;0rad)
  Tip = -> Boolean007
COMPONENT P13 — recipe-attached ("BoardPositive003", modeled in this document).
Construction recipe (the document's own serialized feature program — sketch geometry with constraints, then the solid features built on it; lengths are millimeters unless a unit is written):

FEATURE [Sketcher::SketchObject] Sketch022
  FullyConstrained = true
  MapMode = 5
  Support = -> [XY_Plane019]
  sketch-geometry (5):
    g0: Circle CenterX=-36 CenterY=36 CenterZ=0 NormalX=0 NormalY=0 NormalZ=1 AngleXU=0 Radius=1.62
    g1: LineSegment StartX=-41 StartY=31 StartZ=0 EndX=-31 EndY=31 EndZ=0
    g2: LineSegment StartX=-31 StartY=31 StartZ=0 EndX=-31 EndY=41 EndZ=0
    g3: LineSegment StartX=-31 StartY=41 StartZ=0 EndX=-41 EndY=41 EndZ=0
    g4: LineSegment StartX=-41 StartY=41 StartZ=0 EndX=-41 EndY=31 EndZ=0
  constraints (14):
    c: Radius(g0) = 1.62
    c: Coincident(g1,g2)
    c: Coincident(g2,g3)
    c: Coincident(g3,g4)
    c: Coincident(g4,g1)
    c: Horizontal(g1)
    c: Horizontal(g3)
    c: Vertical(g2)
    c: Vertical(g4)
    c: Equal(g4,g1)
    c: Distance(g2) = 10
    c: Symmetric(g3,g1,g0)
    c: DistanceX(g0,g-1) = 36
    c: DistanceY(g-1,g0) = 36
FEATURE [PartDesign::Pad] Pad014
  Direction = (1,1,1)
  Length = 1.6
  Length2 = 100
  Profile = -> Sketch022
  Refine = true
  Type = 0
FEATURE [PartDesign::Body] Body015  label="BoardPositive003"
  Group = -> [Sketch022,Pad014]
  Origin = -> Origin018
  Placement = pos=(0,0,-0.8) rot=(0,0,1;0rad)
  Tip = -> Pad014
COMPONENT P14 — recipe-attached ("BoardSupport004", modeled in this document).
Construction recipe (the document's own serialized feature program — sketch geometry with constraints, then the solid features built on it; lengths are millimeters unless a unit is written):

FEATURE [Sketcher::SketchObject] Sketch025
  FullyConstrained = true
  MapMode = 5
  Support = -> [XY_Plane020]
  sketch-geometry (5):
    g0: Circle CenterX=-36 CenterY=36 CenterZ=0 NormalX=0 NormalY=0 NormalZ=1 AngleXU=0 Radius=1.62
    g1: LineSegment StartX=-43 StartY=31 StartZ=0 EndX=-31 EndY=31 EndZ=0
    g2: LineSegment StartX=-31 StartY=31 StartZ=0 EndX=-31 EndY=43 EndZ=0
    g3: LineSegment StartX=-31 StartY=43 StartZ=0 EndX=-43 EndY=43 EndZ=0
    g4: LineSegment StartX=-43 StartY=43 StartZ=0 EndX=-43 EndY=31 EndZ=0
  constraints (15):
    c: Radius(g0) = 1.62
    c: Coincident(g1,g2)
    c: Coincident(g2,g3)
    c: Coincident(g3,g4)
    c: Coincident(g4,g1)
    c: Horizontal(g1)
    c: Horizontal(g3)
    c: Vertical(g2)
    c: Vertical(g4)
    c: Equal(g4,g1)
    c: Distance(g2) = 12
    c: DistanceX(g0,g-1) = 36
    c: DistanceY(g-1,g0) = 36
    c: DistanceY(g1,g0) = 5
    c: DistanceX(g0,g1) = 5
FEATURE [PartDesign::Pad] Pad017
  Direction = (1,1,1)
  Length = 5.6
  Length2 = 100
  Midplane = true
  Profile = -> Sketch025
  Refine = true
  Type = 0
FEATURE [PartDesign::Boolean] Boolean008
  BaseFeature = -> Pad017
  Group = -> [Body017]
  Refine = true
  Type = 1
FEATURE [PartDesign::Body] Body016  label="BoardSupport004"
  Group = -> [Sketch025,Pad017,Boolean008]
  Origin = -> Origin019
  Placement = pos=(0,0,24) rot=(0,0,1;0rad)
  Tip = -> Boolean008
COMPONENT P15 — recipe-attached ("BoardPositive004", modeled in this document).
Construction recipe (the document's own serialized feature program — sketch geometry with constraints, then the solid features built on it; lengths are millimeters unless a unit is written):

FEATURE [Sketcher::SketchObject] Sketch024
  FullyConstrained = true
  MapMode = 5
  Support = -> [XY_Plane021]
  sketch-geometry (5):
    g0: Circle CenterX=-36 CenterY=36 CenterZ=0 NormalX=0 NormalY=0 NormalZ=1 AngleXU=0 Radius=1.62
    g1: LineSegment StartX=-41 StartY=31 StartZ=0 EndX=-31 EndY=31 EndZ=0
    g2: LineSegment StartX=-31 StartY=31 StartZ=0 EndX=-31 EndY=41 EndZ=0
    g3: LineSegment StartX=-31 StartY=41 StartZ=0 EndX=-41 EndY=41 EndZ=0
    g4: LineSegment StartX=-41 StartY=41 StartZ=0 EndX=-41 EndY=31 EndZ=0
  constraints (14):
    c: Radius(g0) = 1.62
    c: Coincident(g1,g2)
    c: Coincident(g2,g3)
    c: Coincident(g3,g4)
    c: Coincident(g4,g1)
    c: Horizontal(g1)
    c: Horizontal(g3)
    c: Vertical(g2)
    c: Vertical(g4)
    c: Equal(g4,g1)
    c: Distance(g2) = 10
    c: Symmetric(g3,g1,g0)
    c: DistanceX(g0,g-1) = 36
    c: DistanceY(g-1,g0) = 36
FEATURE [PartDesign::Pad] Pad016
  Direction = (1,1,1)
  Length = 1.6
  Length2 = 100
  Profile = -> Sketch024
  Refine = true
  Type = 0
FEATURE [PartDesign::Body] Body017  label="BoardPositive004"
  Group = -> [Sketch024,Pad016]
  Origin = -> Origin020
  Placement = pos=(0,0,-0.8) rot=(0,0,1;0rad)
  Tip = -> Pad016
COMPONENT P16 — recipe-attached ("Bottom", modeled in this document).
Construction recipe (the document's own serialized feature program — sketch geometry with constraints, then the solid features built on it; lengths are millimeters unless a unit is written):

FEATURE [Sketcher::SketchObject] Sketch004
  FullyConstrained = true
  MapMode = 5
  Support = -> [XY_Plane006]
  sketch-geometry (28):
    g0: LineSegment StartX=-45 StartY=45 StartZ=0 EndX=45 EndY=45 EndZ=0
    g1: LineSegment StartX=45 StartY=45 StartZ=0 EndX=45 EndY=-45 EndZ=0
    g2: LineSegment StartX=45 StartY=-45 StartZ=0 EndX=-45 EndY=-45 EndZ=0
    g3: LineSegment StartX=-45 StartY=-45 StartZ=0 EndX=-45 EndY=45 EndZ=0
    g4: LineSegment StartX=-25 StartY=40 StartZ=0 EndX=25 EndY=40 EndZ=0
    g5: LineSegment StartX=-25 StartY=-40 StartZ=0 EndX=25 EndY=-40 EndZ=0
    g6: LineSegment StartX=-40 StartY=25 StartZ=0 EndX=-40 EndY=-25 EndZ=0
    g7: LineSegment StartX=40 StartY=25 StartZ=0 EndX=40 EndY=-25 EndZ=0
    g8: LineSegment StartX=-31.4645 StartY=28.5355 StartZ=0 EndX=-11.4645 EndY=8.53553 EndZ=0
    g9: LineSegment StartX=-28.5355 StartY=31.4645 StartZ=0 EndX=-8.53553 EndY=11.4645 EndZ=0
    g10: LineSegment StartX=8.53553 StartY=11.4645 StartZ=0 EndX=28.5355 EndY=31.4645 EndZ=0
    g11: LineSegment StartX=31.4645 StartY=28.5355 StartZ=0 EndX=11.4645 EndY=8.53553 EndZ=0
    g12: LineSegment StartX=11.4645 StartY=-8.53553 StartZ=0 EndX=31.4645 EndY=-28.5355 EndZ=0
    g13: LineSegment StartX=28.5355 StartY=-31.4645 StartZ=0 EndX=8.53553 EndY=-11.4645 EndZ=0
    g14: LineSegment StartX=-8.53553 StartY=-11.4645 StartZ=0 EndX=-28.5355 EndY=-31.4645 EndZ=0
    g15: LineSegment StartX=-31.4645 StartY=-28.5355 StartZ=0 EndX=-11.4645 EndY=-8.53553 EndZ=0
    g16: ArcOfCircle CenterX=35 CenterY=25 CenterZ=0 NormalX=0 NormalY=0 NormalZ=1 AngleXU=0 Radius=5 StartAngle=0 EndAngle=2.35619
    g17: ArcOfCircle CenterX=35 CenterY=-25 CenterZ=0 NormalX=0 NormalY=0 NormalZ=1 AngleXU=0 Radius=5 StartAngle=3.92699 EndAngle=6.28319
    g18: ArcOfCircle CenterX=25 CenterY=-35 CenterZ=0 NormalX=0 NormalY=0 NormalZ=1 AngleXU=0 Radius=5 StartAngle=4.71239 EndAngle=7.06858
    g19: ArcOfCircle CenterX=-25 CenterY=-35 CenterZ=0 NormalX=0 NormalY=0 NormalZ=1 AngleXU=0 Radius=5 StartAngle=2.35619 EndAngle=4.71239
    g20: ArcOfCircle CenterX=-35 CenterY=-25 CenterZ=0 NormalX=0 NormalY=0 NormalZ=1 AngleXU=0 Radius=5 StartAngle=3.14159 EndAngle=5.49779
    g21: ArcOfCircle CenterX=-35 CenterY=25 CenterZ=0 NormalX=0 NormalY=0 NormalZ=1 AngleXU=0 Radius=5 StartAngle=0.785398 EndAngle=3.14159
    g22: ArcOfCircle CenterX=-25 CenterY=35 CenterZ=0 NormalX=0 NormalY=0 NormalZ=1 AngleXU=0 Radius=5 StartAngle=1.5708 EndAngle=3.92699
    g23: ArcOfCircle CenterX=25 CenterY=35 CenterZ=0 NormalX=0 NormalY=0 NormalZ=1 AngleXU=0 Radius=5 StartAngle=5.49779 EndAngle=7.85398
    g24: ArcOfCircle CenterX=-20 CenterY=0 CenterZ=0 NormalX=0 NormalY=0 NormalZ=1 AngleXU=0 Radius=12.0711 StartAngle=5.49779 EndAngle=7.06858
    g25: ArcOfCircle CenterX=0 CenterY=20 CenterZ=0 NormalX=0 NormalY=0 NormalZ=1 AngleXU=0 Radius=12.0711 StartAngle=3.92699 EndAngle=5.49779
    g26: ArcOfCircle CenterX=20 CenterY=0 CenterZ=0 NormalX=0 NormalY=0 NormalZ=1 AngleXU=0 Radius=12.0711 StartAngle=2.35619 EndAngle=3.92699
    g27: ArcOfCircle CenterX=1.6498e-12 CenterY=-20 CenterZ=0 NormalX=0 NormalY=0 NormalZ=1 AngleXU=0 Radius=12.0711 StartAngle=0.785398 EndAngle=2.35619
  constraints (67):
    c: Coincident(g0,g1)
    c: Coincident(g1,g2)
    c: Coincident(g2,g3)
    c: Coincident(g3,g0)
    c: Horizontal(g0)
    c: Horizontal(g2)
    c: Vertical(g1)
    c: Vertical(g3)
    c: Symmetric(g0,g1,g-1)
    c: Equal(g2,g1)
    c: Horizontal(g4)
    c: Horizontal(g5)
    c: Vertical(g6)
    c: Vertical(g7)
    c: DistanceY(g3,g3) = 90
    c: Parallel(g8,g9)
    c: Parallel(g9,g12)
    c: Parallel(g12,g13)
    c: Parallel(g15,g14)
    c: Parallel(g14,g10)
    c: Parallel(g10,g11)
    c: Tangent(g11,g16) = -1.5708
    c: Tangent(g7,g16) = 1.5708
    c: Tangent(g12,g17) = -1.5708
    c: Tangent(g7,g17) = 1.5708
    c: Tangent(g13,g18) = -1.5708
    c: Tangent(g5,g18) = -1.5708
    c: Tangent(g14,g19) = -1.5708
    c: Tangent(g5,g19) = -1.5708
    c: Tangent(g15,g20) = -1.5708
    c: Tangent(g6,g20) = -1.5708
    c: Tangent(g6,g21) = -1.5708
    c: Tangent(g8,g21) = 1.5708
    c: Tangent(g9,g22) = -1.5708
    c: Tangent(g4,g22) = 1.5708
    c: Tangent(g4,g23) = 1.5708
    c: Tangent(g10,g23) = -1.5708
    c: Tangent(g8,g24) = 1.5708
    c: Tangent(g15,g24) = -1.5708
    c: Tangent(g9,g25) = -1.5708
    c: Tangent(g10,g25) = -1.5708
    c: Tangent(g11,g26) = -1.5708
    c: Tangent(g12,g26) = -1.5708
    c: Tangent(g13,g27) = -1.5708
    c: Tangent(g14,g27) = -1.5708
    c: Symmetric(g8,g12,g-1)
    c: PointOnObject(g24,g-1)
    c: PointOnObject(g26,g-1)
    c: Symmetric(g10,g14,g-1)
    c: Symmetric(g21,g17,g-1)
    c: Symmetric(g19,g23,g-1)
    c: Vertical(g21,g20)
    c: Horizontal(g18,g19)
    c: Vertical(g15,g8)
    c: Equal(g25,g24)
    c: Equal(g26,g27)
    c: PointOnObject(g25,g-2)
    c: Horizontal(g16,g21)
    c: Equal(g4,g5)
    c: Equal(g6,g5)
    c: DistanceX(g2,g6) = 5
    c: DistanceY(g2,g5) = 5
    c: DistanceX(g18,g1) = 20
    c: DistanceX(g26,g1) = 25
    c: DistanceY(g1,g18) = 10
    c: Perpendicular(g11,g8)
    c: DistanceX(g17,g1) = 10
FEATURE [PartDesign::Pad] Pad004
  Direction = (1,1,1)
  Length = 5
  Length2 = 100
  Profile = -> Sketch004
  Refine = true
  Type = 0
FEATURE [Sketcher::SketchObject] Sketch009  label="topLeftHoleSketch"
  FullyConstrained = true
  MapMode = 5
  Placement = pos=(0,0,-10) rot=(0,0,1;0rad)
  Support = -> [Hole]
  sketch-geometry (1):
    g0: Circle CenterX=-36 CenterY=36 CenterZ=0 NormalX=0 NormalY=0 NormalZ=1 AngleXU=0 Radius=2
  constraints (3):
    c: DistanceX(g-1,g0) = -36
    c: DistanceY(g-1,g0) = 36
    c: Radius(g0) = 2
FEATURE [PartDesign::Hole] Hole004  label="topLeftHole"
  BaseFeature = -> Pad004
  Depth = 25
  DepthType = 1
  Diameter = 4
  DrillForDepth = false
  DrillPoint = 1
  DrillPointAngle = 118
  HoleCutCountersinkAngle = 90
  HoleCutCustomValues = false
  HoleCutDepth = 0
  HoleCutDiameter = 6.1
  HoleCutType = 0
  ModelActualThread = false
  Profile = -> Sketch009
  Refine = true
  Reversed = true
  Tapered = false
  TaperedAngle = 90
  ThreadAngle = 0
  ThreadClass = 0
  ThreadCutOffInner = 0
  ThreadCutOffOuter = 0
  ThreadDirection = 0
  ThreadFit = 0
  ThreadPitch = 0
  ThreadSize = 0
  ThreadType = 0
  Threaded = false
FEATURE [PartDesign::Mirrored] Mirrored001
  MirrorPlane = -> Sketch009 [V_Axis]
  Refine = true
FEATURE [PartDesign::Mirrored] Mirrored002
  MirrorPlane = -> Sketch009 [H_Axis]
  Refine = true
FEATURE [PartDesign::MultiTransform] MultiTransform001
  BaseFeature = -> Hole004
  Originals = -> [Hole004]
  Refine = true
  Transformations = -> [Mirrored001,Mirrored002]
FEATURE [PartDesign::Body] Body004  label="Plate001"
  Group = -> [Sketch004,Pad004,Sketch009,Hole004,MultiTransform001,Mirrored001,Mirrored002]
  Origin = -> Origin006
  Placement = pos=(0,0,5) rot=(0,0,1;0rad)
  Tip = -> MultiTransform001
COMPONENT P17 — recipe-attached ("Side", modeled in this document).
Construction recipe (the document's own serialized feature program — sketch geometry with constraints, then the solid features built on it; lengths are millimeters unless a unit is written):

FEATURE [Sketcher::SketchObject] Sketch001
  FullyConstrained = true
  MapMode = 5
  Support = -> [XY_Plane003]
  sketch-geometry (8):
    g0: LineSegment StartX=-49 StartY=50 StartZ=0 EndX=-41 EndY=50 EndZ=0
    g1: LineSegment StartX=-40 StartY=49 StartZ=0 EndX=-40 EndY=41 EndZ=0
    g2: LineSegment StartX=-41 StartY=40 StartZ=0 EndX=-49 EndY=40 EndZ=0
    g3: LineSegment StartX=-50 StartY=41 StartZ=0 EndX=-50 EndY=49 EndZ=0
    g4: ArcOfCircle CenterX=-49 CenterY=41 CenterZ=0 NormalX=0 NormalY=0 NormalZ=1 AngleXU=0 Radius=1 StartAngle=3.14159 EndAngle=4.71239
    g5: ArcOfCircle CenterX=-41 CenterY=41 CenterZ=0 NormalX=0 NormalY=0 NormalZ=1 AngleXU=0 Radius=1 StartAngle=4.71239 EndAngle=6.28319
    g6: ArcOfCircle CenterX=-41 CenterY=49 CenterZ=0 NormalX=0 NormalY=0 NormalZ=1 AngleXU=0 Radius=1 StartAngle=7.1e-14 EndAngle=1.5708
    g7: ArcOfCircle CenterX=-49 CenterY=49 CenterZ=0 NormalX=0 NormalY=0 NormalZ=1 AngleXU=0 Radius=1 StartAngle=1.5708 EndAngle=3.14159
  constraints (20):
    c: Horizontal(g0)
    c: Horizontal(g2)
    c: Vertical(g1)
    c: Vertical(g3)
    c: Equal(g3,g2)
    c: Tangent(g3,g4) = 1.5708
    c: Tangent(g2,g4) = 1.5708
    c: Tangent(g2,g5) = 1.5708
    c: Tangent(g1,g5) = 1.5708
    c: Tangent(g1,g6) = 1.5708
    c: Tangent(g0,g6) = 1.5708
    c: Tangent(g3,g7) = 1.5708
    c: Tangent(g0,g7) = 1.5708
    c: Equal(g7,g6)
    c: Equal(g6,g5)
    c: Equal(g5,g4)
    c: DistanceY(g2,g0) = 10
    c: Radius(g4) = 1
    c: DistanceY(g-1,g2) = 40
    c: DistanceX(g1,g-1) = 40
FEATURE [PartDesign::Pad] Pad001  label="padHeight"
  Direction = (1,1,1)
  Length = 100
  Length2 = 100
  Profile = -> Sketch001
  Refine = true
  Type = 0
FEATURE [PartDesign::Boolean] Boolean  label="PlateCutouts"
  BaseFeature = -> Pad001
  Group = -> [Body,Body005]
  Refine = true
  Type = 1
FEATURE [PartDesign::Boolean] Boolean002  label="boolWithPlateSupport"
  BaseFeature = -> Boolean
  Group = -> [Body002,Body006]
  Refine = true
  Type = 0
FEATURE [PartDesign::Boolean] Boolean009  label="boolWithBoardSupport"
  BaseFeature = -> Boolean002
  Group = -> [Body008,Body010,Body012,Body014,Body016]
  Refine = true
  Type = 0
FEATURE [PartDesign::Body] Body001  label="Post"
  Group = -> [Sketch001,Pad001,Boolean,Boolean002,Boolean009]
  Origin = -> Origin003
  Tip = -> Boolean009
PROVENANCE & LICENSES
A FreeCAD (.FCStd) document from a public repository crawl; recipes are the document's own serialized feature recipes (and, for linked parts, companion documents' recipes).
License: as declared in the source repository (recorded in the dataset sidecar).
